# Revit family: Reece_Tap_Mizu_Drift_Bath Hob Outlet_Gooseneck
name_source: partatom
category: Plumbing Fixtures
revit_build: Autodesk Revit 2018 (Build: 20180329_1100(x64)
units: mm (PartAtom-declared; Revit-internal decimal feet)

## family parameters
Cut with Voids When Loaded = No
Host = Face
Part Type = Normal
Room Calculation Point = Yes
Round Connector Dimension = Use Diameter
Shared = Yes

## types (1)
- 210 mm_Chrome
    CWFU = 0
    Default Elevation = 1000 mm
    Description = Bath Hob Outlet
    Disclaimer = THIS FILE IS THE PROPERTY OF THE REECE GROUP. IT MAY NOT BE REPRODUCED, REVERSE-ENGINEERED OR MODIFIED. ANY REPUBLICATION, TRANSMISSION OR DISTRIBUTION FOR THE PURPOSE OF COMMERCIALLY EXPLOITING THE FILES IS PROHIBITED.
    HWFU = 0
    Keynote = Product #9503823, Reece_Tap_Mizu_Drift_Bath Hob Outlet_Gooseneck - 210 mm_Chrome
    Manufacturer = Mizu
    Model = Drift
    Reece_Base_Plate_Radius = 25 mm  [stored 0.082021 ft]
    Reece_Detail_Disclaimer = THIS FILE IS THE PROPERTY OF THE REECE GROUP. IT MAY NOT BE REPRODUCED, REVERSE-ENGINEERED OR MODIFIED. ANY REPUBLICATION, TRANSMISSION OR DISTRIBUTION FOR THE PURPOSE OF COMMERCIALLY EXPLOITING THE FILES IS PROHIBITED.
    Reece_Detail_Shape = Gooseneck
    Reece_Material_Main = Reece_Brass_Chrome
    Reece_Overall_Height = 235 mm  [stored 0.770997 ft]
    Reece_Overall_Length = 249 mm
    Reece_Product_Brand = Mizu
    Reece_Product_Description = Mizu Drift Gooseneck Hob Bath Outlet Chrome
    Reece_Product_Mount = Hob Mounted
    Reece_Product_Number = 9503823
    Reece_Product_Sub Brand = Drift
    Reece_Product_Type = Tap
    Reece_Product_Web Page = https://www.reece.com.au
    Reece_Tap_Clearance = 153 mm
    Reece_Tap_Inlet = 14 mm  [stored 0.0459318 ft]
    Reece_Tap_Reach = 210 mm  [stored 0.688976 ft]
    Type Comments = Tap
    URL = https://www.reece.com.au
    WFU = 0

note: [stored X ft] marks values corroborated as IEEE doubles in the binary element streams (Revit-internal decimal feet)

## geometry (parser evidence)
native form markers: Sweep x2
no freeform markers — native parametric forms only
